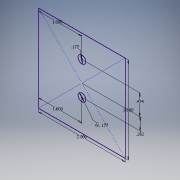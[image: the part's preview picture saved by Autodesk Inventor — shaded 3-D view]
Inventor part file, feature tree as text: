
AUTODESK INVENTOR PART (.ipt)
format: ipt  version: 2016 (Build 200138000, 138)  size: 90,624 bytes
history: native  units: in
note: dims shown in document units (in); Inventor stores cm internally (conversion verified against a paired STEP export)
features: sketch x1
ambient origin geometry x8: Origin, YZ Plane, XZ Plane, XY Plane, X Axis, Y Axis, Z Axis, Center Point
feature tree (1):
  sketch  "Sketch1"  dims[d0=2.0in d1=2.0in d5=0.177in d6=0.474in d7=1.0in d8=0.177in d9=1.0in d10=0.2823in]
